# Revit family: IB_Precast-I Shaped Beam_Spæncom
name_source: partatom
category: Structural Framing
revit_build: Autodesk Revit 2014 (Build: 20130308_1515(x64)
units: mm (PartAtom-declared; Revit-internal decimal feet)

## types (12) — shared parameters
Manufacturer = Spæncom

## per-type parameters (varying)
| type | Height element | Length RB-Profile (minimum value equals element height) | Mirror Depth end | Mirror base IB | Mirror base RB | Mirror thickness | Mirror top IB | Mirror top RB | Model | Width element |
| IB30/60 | 600 mm  [stored 1.9685 ft] | 600 mm  [stored 1.9685 ft] | 110 mm  [stored 0.360892 ft] | 110 mm  [stored 0.360892 ft] | 80 mm  [stored 0.262467 ft] | 80 mm  [stored 0.262467 ft] | 80 mm  [stored 0.262467 ft] | 100 mm  [stored 0.328084 ft] | IB30/60 | 300 mm |
| IB36/60 | 600 mm  [stored 1.9685 ft] | 600 mm  [stored 1.9685 ft] | 110 mm  [stored 0.360892 ft] | 110 mm  [stored 0.360892 ft] | 80 mm  [stored 0.262467 ft] | 140 mm  [stored 0.459318 ft] | 80 mm  [stored 0.262467 ft] | 100 mm  [stored 0.328084 ft] | IB 36/60 | 360 mm  [stored 1.1811 ft] |
| IB30/72 | 720 mm  [stored 2.3622 ft] | 720 mm  [stored 2.3622 ft] | 110 mm  [stored 0.360892 ft] | 110 mm  [stored 0.360892 ft] | 80 mm  [stored 0.262467 ft] | 80 mm  [stored 0.262467 ft] | 80 mm  [stored 0.262467 ft] | 120 mm  [stored 0.393701 ft] | IB 30/72 | 300 mm |
| IB36/72 | 720 mm  [stored 2.3622 ft] | 720 mm  [stored 2.3622 ft] | 110 mm  [stored 0.360892 ft] | 110 mm  [stored 0.360892 ft] | 80 mm  [stored 0.262467 ft] | 140 mm  [stored 0.459318 ft] | 80 mm  [stored 0.262467 ft] | 120 mm  [stored 0.393701 ft] | IB 36/72 | 360 mm  [stored 1.1811 ft] |
| IB30/84 | 840 mm  [stored 2.75591 ft] | 840 mm  [stored 2.75591 ft] | 100 mm  [stored 0.328084 ft] | 100 mm  [stored 0.328084 ft] | 100 mm  [stored 0.328084 ft] | 100 mm  [stored 0.328084 ft] | 100 mm  [stored 0.328084 ft] | 100 mm  [stored 0.328084 ft] | IB 30/84 | 300 mm |
| IB36/84 | 840 mm  [stored 2.75591 ft] | 840 mm  [stored 2.75591 ft] | 100 mm  [stored 0.328084 ft] | 100 mm  [stored 0.328084 ft] | 100 mm  [stored 0.328084 ft] | 160 mm  [stored 0.524934 ft] | 100 mm  [stored 0.328084 ft] | 100 mm  [stored 0.328084 ft] | IB 36/84 | 360 mm  [stored 1.1811 ft] |
| IB30/108 | 1080 mm  [stored 3.54331 ft] | 1080 mm  [stored 3.54331 ft] | 100 mm  [stored 0.328084 ft] | 100 mm  [stored 0.328084 ft] | 100 mm  [stored 0.328084 ft] | 100 mm  [stored 0.328084 ft] | 100 mm  [stored 0.328084 ft] | 100 mm  [stored 0.328084 ft] | IB 30/108 | 300 mm |
| IB36/108 | 1080 mm  [stored 3.54331 ft] | 1080 mm  [stored 3.54331 ft] | 100 mm  [stored 0.328084 ft] | 100 mm  [stored 0.328084 ft] | 100 mm  [stored 0.328084 ft] | 160 mm  [stored 0.524934 ft] | 100 mm  [stored 0.328084 ft] | 100 mm  [stored 0.328084 ft] | IB 36/108 | 360 mm  [stored 1.1811 ft] |
| IB30/120 | 1200 mm | 1200 mm | 100 mm  [stored 0.328084 ft] | 100 mm  [stored 0.328084 ft] | 100 mm  [stored 0.328084 ft] | 100 mm  [stored 0.328084 ft] | 100 mm  [stored 0.328084 ft] | 100 mm  [stored 0.328084 ft] | IB 30/120 | 300 mm |
| IB36/120 | 1200 mm | 1200 mm | 100 mm  [stored 0.328084 ft] | 100 mm  [stored 0.328084 ft] | 100 mm  [stored 0.328084 ft] | 160 mm  [stored 0.524934 ft] | 100 mm  [stored 0.328084 ft] | 100 mm  [stored 0.328084 ft] | IB 36/120 | 360 mm  [stored 1.1811 ft] |
| IB36/132 | 1320 mm | 1320 mm | 120 mm  [stored 0.393701 ft] | 120 mm  [stored 0.393701 ft] | 100 mm  [stored 0.328084 ft] | 120 mm  [stored 0.393701 ft] | 60 mm  [stored 0.19685 ft] | 200 mm  [stored 0.656168 ft] | IB 36/132 | 360 mm  [stored 1.1811 ft] |
| IB42/132 | 1320 mm | 1320 mm | 120 mm  [stored 0.393701 ft] | 120 mm  [stored 0.393701 ft] | 100 mm  [stored 0.328084 ft] | 180 mm  [stored 0.590551 ft] | 60 mm  [stored 0.19685 ft] | 200 mm  [stored 0.656168 ft] | IB 42/132 | 420 mm  [stored 1.37795 ft] |

note: [stored X ft] marks values corroborated as IEEE doubles in the binary element streams (Revit-internal decimal feet)

## geometry (parser evidence)
native form markers: Sweep x6
no freeform markers — native parametric forms only
